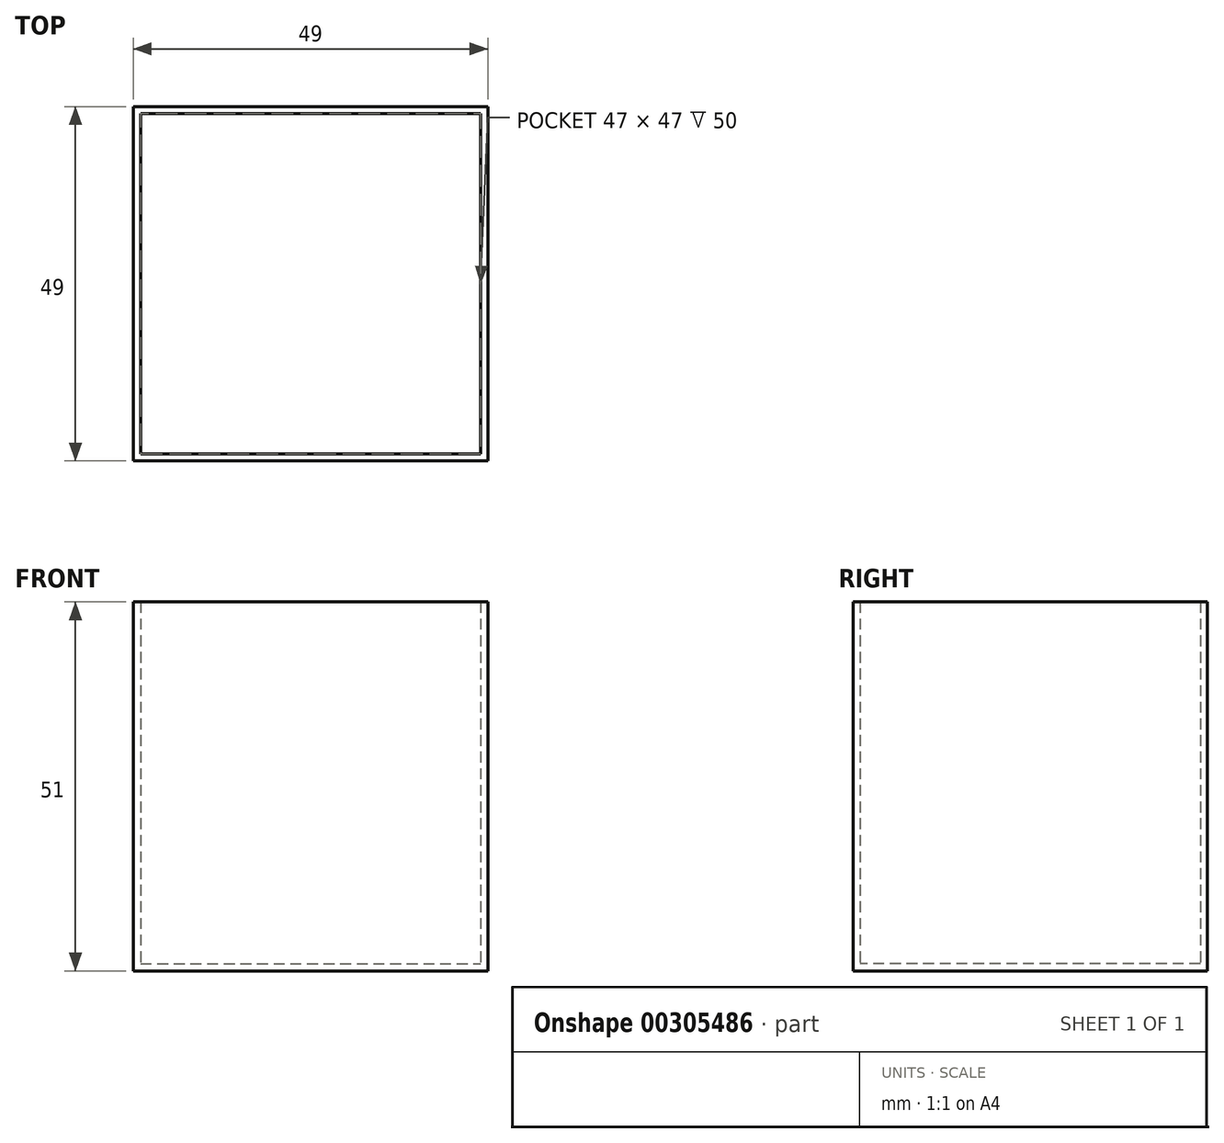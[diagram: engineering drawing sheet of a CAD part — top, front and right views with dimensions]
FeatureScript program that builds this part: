
annotation { "Feature Type Name" : "Feature", "Feature Type Description" : "" }
export const myFeature = defineFeature(function(context is Context, id is Id, definition is map)
    precondition{}
    {
        {
            var Q0;
            Q0=qCreatedBy(makeId("Top.planeOp"),FACE);
            var sketch = newSketch(context, id + "F0", { "sketchPlane" : qUnion([Q0])});
            skLineSegment(sketch, "E0.bottom", {"start": v(-24.5, 24.5) * mm, "end": v(24.5, 24.5) * mm});
            skLineSegment(sketch, "E0.top", {"start": v(-24.5, -24.5) * mm, "end": v(24.5, -24.5) * mm});
            skLineSegment(sketch, "E0.left", {"start": v(-24.5, 24.5) * mm, "end": v(-24.5, -24.5) * mm});
            skLineSegment(sketch, "E0.right", {"start": v(24.5, 24.5) * mm, "end": v(24.5, -24.5) * mm});
            skLineSegment(sketch, "E1", {"start": v(0, 34.35) * mm, "end": v(0, -55.86) * mm, "construction": true});
            skLineSegment(sketch, "E2", {"start": v(40.63, 0) * mm, "end": v(-57.36, 0) * mm, "construction": true});
            skLineSegment(sketch, "E3.0", {"start": v(-23.5, 23.5) * mm, "end": v(23.5, 23.5) * mm});
            skLineSegment(sketch, "E3.1", {"start": v(-23.5, 23.5) * mm, "end": v(-23.5, -23.5) * mm});
            skLineSegment(sketch, "E3.2", {"start": v(-23.5, -23.5) * mm, "end": v(23.5, -23.5) * mm});
            skLineSegment(sketch, "E3.3", {"start": v(23.5, 23.5) * mm, "end": v(23.5, -23.5) * mm});
            skSolve(sketch);
        }
        {
            var Q0;
            Q0=makeQuery(id+"F0.imprint","IMPRINT",FACE,{"disambiguationData":[TD([[makeQuery(id+"F0.imprint","IMPRINT",EDGE,{"derivedFrom":sQuery(id+"F0.wireOp",EDGE,"E3.0")}),-1.0]])]});
            var Q1;
            Q1=makeQuery(id+"F0.imprint","IMPRINT",FACE,{"disambiguationData":[TD([[makeQuery(id+"F0.imprint","IMPRINT",EDGE,{"derivedFrom":sQuery(id+"F0.wireOp",EDGE,"E0.bottom")}),-1.0]])]});
            extrude(context, id + "F1", {"entities" : qUnion([Q0, Q1]), "oppositeDirection" : true, "depth" : 1 * mm});
        }
        {
            var Q0;
            Q0=makeQuery(id+"F0.imprint","IMPRINT",FACE,{"disambiguationData":[TD([[makeQuery(id+"F0.imprint","IMPRINT",EDGE,{"derivedFrom":sQuery(id+"F0.wireOp",EDGE,"E0.bottom")}),-1.0]])]});
            extrude(context, id + "F2", {"entities" : qUnion([Q0]), "operationType" : NewBodyOperationType.ADD, "depth" : 50 * mm});
        }
    });
